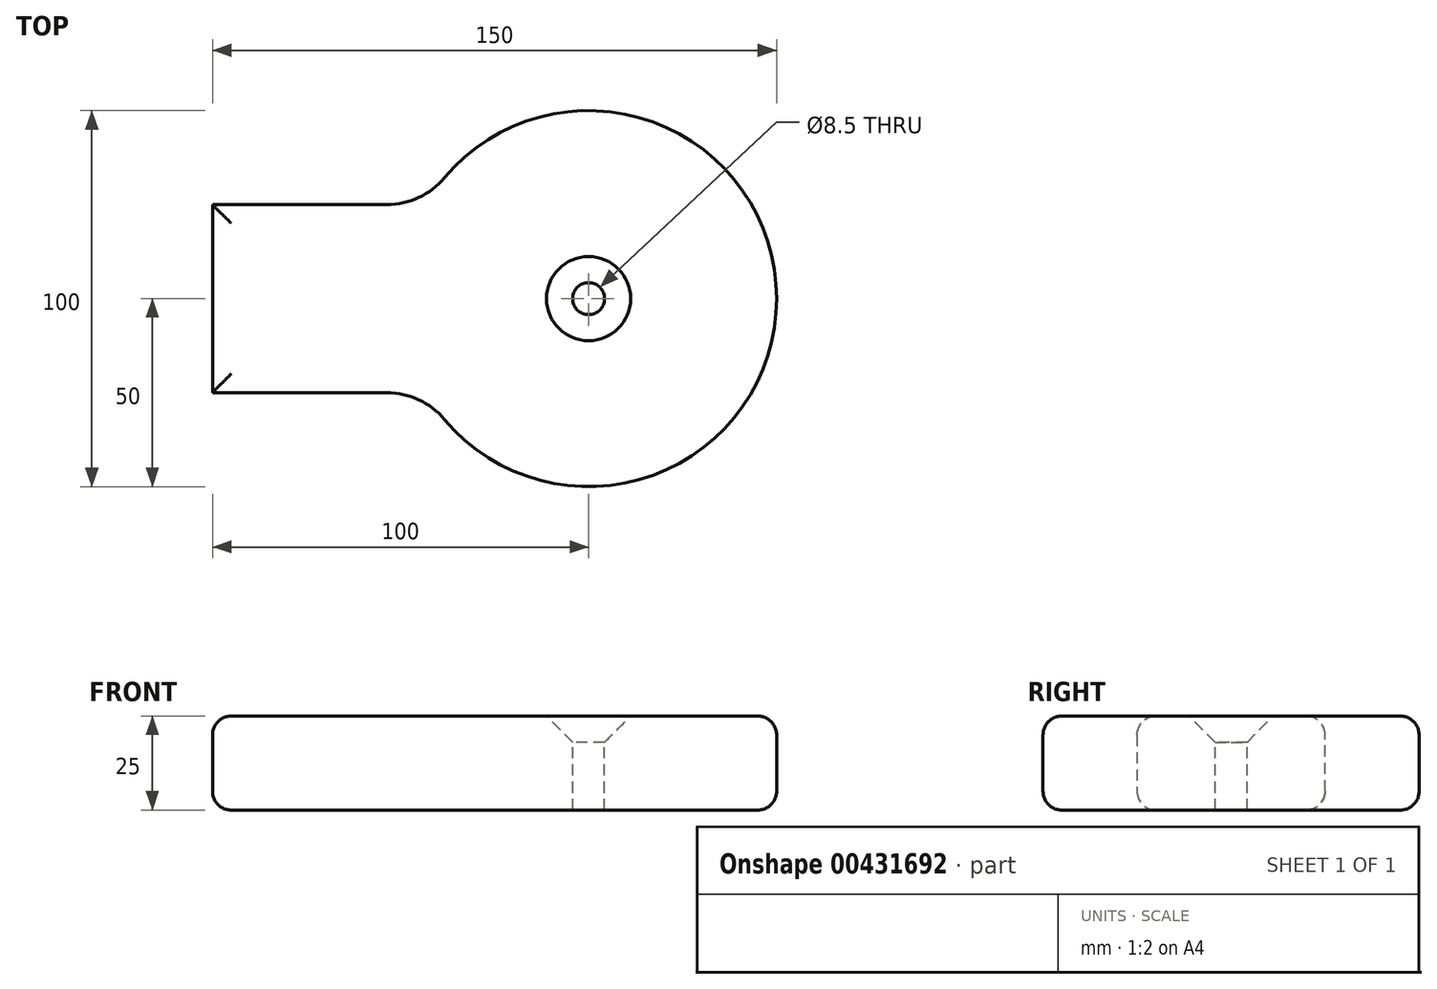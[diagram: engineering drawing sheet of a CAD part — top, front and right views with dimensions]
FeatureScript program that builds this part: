
annotation { "Feature Type Name" : "Feature", "Feature Type Description" : "" }
export const myFeature = defineFeature(function(context is Context, id is Id, definition is map)
    precondition{}
    {
        {
            var Q0;
            Q0=qCreatedBy(makeId("Top.planeOp"),FACE);
            var sketch = newSketch(context, id + "F0", { "sketchPlane" : qUnion([Q0])});
            skCircle(sketch, "E0", {"center": v(0, 0) * mm, "radius": 50 * mm});
            skLineSegment(sketch, "E1", {"start": v(-43.3, 25) * mm, "end": v(-100, 25) * mm});
            skLineSegment(sketch, "E2", {"start": v(-100, 25) * mm, "end": v(-100, -25) * mm});
            skLineSegment(sketch, "E3", {"start": v(-100, -25) * mm, "end": v(-43.3, -25) * mm});
            skLineSegment(sketch, "E4", {"start": v(-100, 0) * mm, "end": v(0, 0) * mm, "construction": true});
            skSolve(sketch);
        }
        {
            var Q0;
            {var subQ0=sQuery(id+"F0.wireOp",EDGE,"E1");Q0=makeQuery(id+"F0.imprint","IMPRINT",FACE,{"disambiguationData":[TD([[makeQuery(id+"F0.imprint","IMPRINT",EDGE,{"derivedFrom":subQ0}),1.0]])]});}
            var Q1;
            {var subQ0=sQuery(id+"F0.wireOp",EDGE,"E0");var subQ1=makeQuery(id+"F0.imprint","INTERSECT",VERTEX,{"derivedFrom":[subQ0,sQuery(id+"F0.wireOp",EDGE,"E1")]});Q1=makeQuery(id+"F0.imprint","IMPRINT",FACE,{"disambiguationData":[TD([[makeQuery(id+"F0.imprint","IMPRINT",EDGE,{"disambiguationData":[TD([[subQ1,-1.0]])],"derivedFrom":subQ0}),1.0]])]});}
            var Q2;
            Q2=sQuery(id+"F0.wireOp",EDGE,"E0");
            var Q3;
            Q3=sQuery(id+"F0.wireOp",EDGE,"E1");
            var Q4;
            Q4=sQuery(id+"F0.wireOp",EDGE,"E2");
            var Q5;
            Q5=sQuery(id+"F0.wireOp",EDGE,"E3");
            extrude(context, id + "F1", {"entities" : qUnion([Q0, Q1]), "surfaceEntities" : qUnion([Q2, Q3, Q4, Q5]), "endBound" : BoundingType.SYMMETRIC, "depth" : 25 * mm});
        }
        {
            var Q0;
            Q0=makeQuery(id+"F1.opExtrude","SWEPT_EDGE",EDGE,{"disambiguationData":[OSD([sQuery(id+"F0.wireOp",EDGE,"E0"),sQuery(id+"F0.wireOp",EDGE,"E3")])]});
            var Q1;
            Q1=makeQuery(id+"F1.opExtrude","SWEPT_EDGE",EDGE,{"disambiguationData":[OSD([sQuery(id+"F0.wireOp",EDGE,"E0"),sQuery(id+"F0.wireOp",EDGE,"E1")])]});
            fillet(context, id + "F2", {"entities" : qUnion([Q0, Q1]), "radius" : 20 * mm, "tangentPropagation" : true, "allowEdgeOverflow" : false});
        }
        {
            var Q0;
            Q0=makeQuery(id+"F1.opExtrude","CAP_FACE",FACE,{"disambiguationData":[OSD([sQuery(id+"F0.wireOp",EDGE,"E0"),sQuery(id+"F0.wireOp",EDGE,"E1"),sQuery(id+"F0.wireOp",EDGE,"E2"),sQuery(id+"F0.wireOp",EDGE,"E3")])],"isStart":false});
            var Q1;
            Q1=makeQuery(id+"F1.opExtrude","CAP_FACE",FACE,{"disambiguationData":[OSD([sQuery(id+"F0.wireOp",EDGE,"E0"),sQuery(id+"F0.wireOp",EDGE,"E1"),sQuery(id+"F0.wireOp",EDGE,"E2"),sQuery(id+"F0.wireOp",EDGE,"E3")])],"isStart":true});
            fillet(context, id + "F3", {"entities" : qUnion([Q0, Q1]), "radius" : 5 * mm, "tangentPropagation" : true, "allowEdgeOverflow" : false});
        }
        {
            var Q0;
            Q0=makeQuery(id+"F1.opExtrude","CAP_FACE",FACE,{"disambiguationData":[OSD([sQuery(id+"F0.wireOp",EDGE,"E0"),sQuery(id+"F0.wireOp",EDGE,"E1"),sQuery(id+"F0.wireOp",EDGE,"E2"),sQuery(id+"F0.wireOp",EDGE,"E3")])],"isStart":false});
            var sketch = newSketch(context, id + "F4", { "sketchPlane" : qUnion([Q0])});
            skPoint(sketch, "E5", {"position": v(0, 0) * mm});
            skSolve(sketch);
        }
        {
            var Q0;
            Q0=sQuery(id+"F4.wireOp",VERTEX,"E5");
            var Q1;
            Q1=makeQuery(id+"F1.opExtrude","SWEPT_BODY",BODY,{"disambiguationData":[OSD([sQuery(id+"F0.wireOp",EDGE,"E0"),sQuery(id+"F0.wireOp",EDGE,"E1"),sQuery(id+"F0.wireOp",EDGE,"E2"),sQuery(id+"F0.wireOp",EDGE,"E3")])]});
            hole(context, id + "F5", {"style" : HoleStyle.C_SINK, "endStyle" : HoleEndStyle.THROUGH, "standardTappedOrClearance" : lookupTablePath({ "standard" : "ISO", "engagement" : "75%", "pitch" : "1.5 mm", "size" : "M10", "type" : "Tapped" }), "standardBlindInLast" : lookupTablePath({ "standard" : "ISO", "engagement" : "75%", "pitch" : "1.5 mm", "size" : "M10", "type" : "Tapped" }), "holeDiameter" : 8.5 * mm, "cSinkDiameter" : 22.4 * mm, "cSinkAngle" : 90 * degree, "showTappedDepth" : true, "isTappedThrough" : true, "tappedDepth" : 12 * mm, "tapClearance" : 3, "startFromSketch" : true, "locations" : qUnion([Q0]), "scope" : qUnion([Q1]), "majorDiameter" : 10 * mm});
        }
    });
